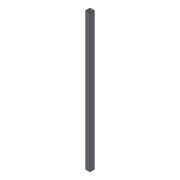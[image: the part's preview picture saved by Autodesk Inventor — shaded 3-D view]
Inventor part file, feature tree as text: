
AUTODESK INVENTOR PART (.ipt)
format: ipt  version: 2012 (Build 160160000, 160)  size: 71,680 bytes
history: native  units: in
note: dims shown in document units (in); Inventor stores cm internally (conversion verified against a paired STEP export)
features: extrude x1, shell x1, sketch x1
ambient origin geometry x8: Origin, YZ Plane, XZ Plane, XY Plane, X Axis, Y Axis, Z Axis, Center Point
bodies: Solid1 (feature_tree)
feature tree (3):
  extrude  "Extrusion1"  Depth=30.0in
  shell  "Shell1"  Thickness=1.0in
  sketch  "Sketch1"  dims[d0=1.0in d1=30.0in d2=1.0in d3=0.0in d4=0.0625in]
